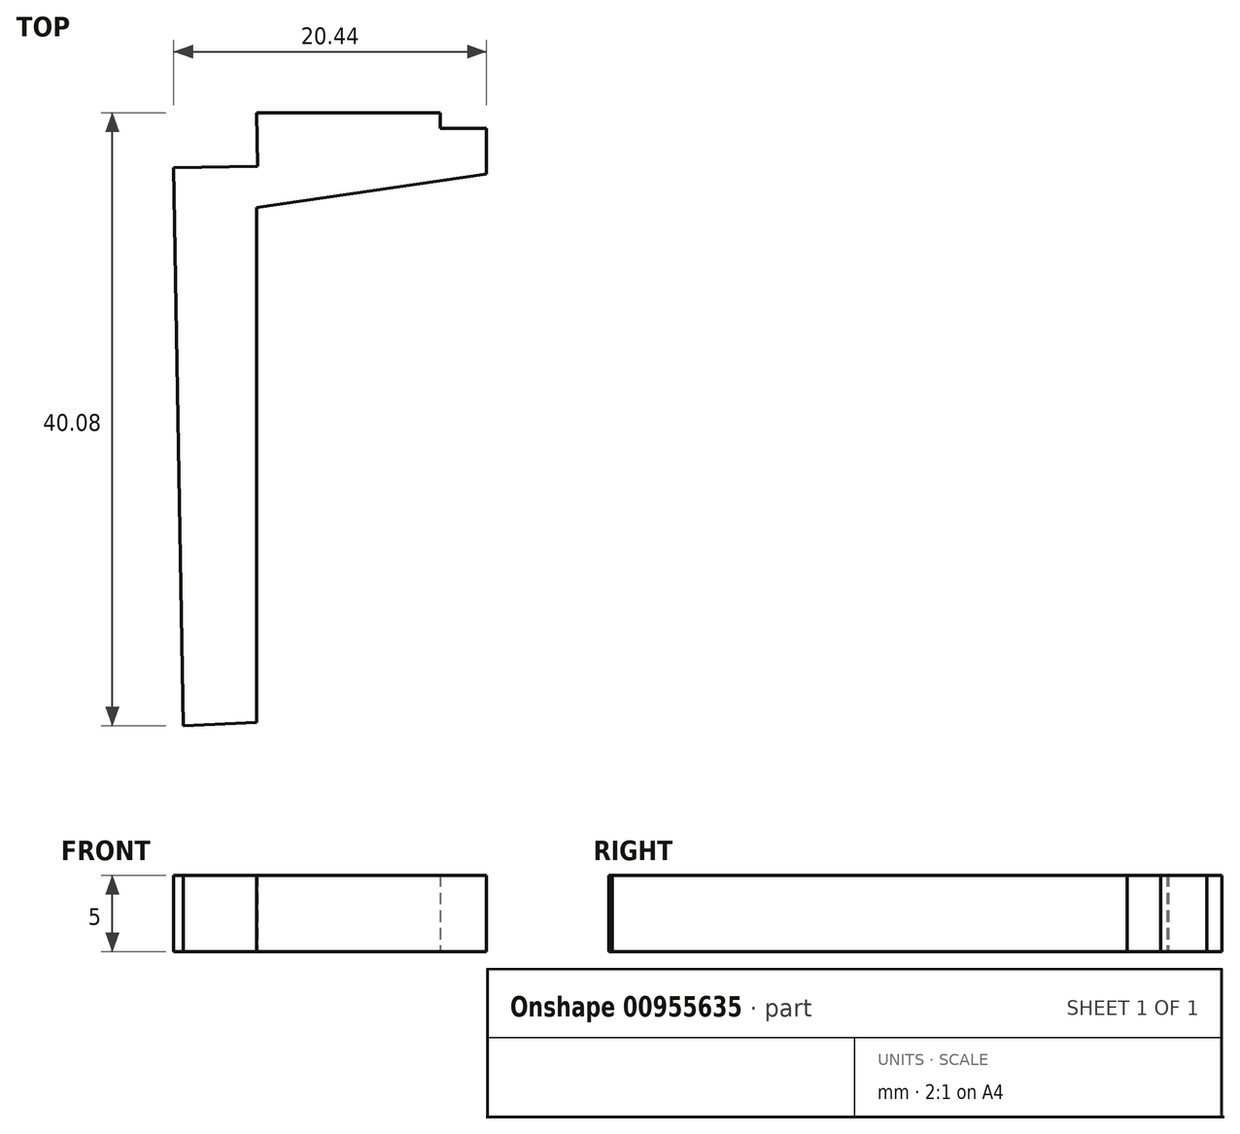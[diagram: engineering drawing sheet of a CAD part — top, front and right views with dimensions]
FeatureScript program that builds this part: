
annotation { "Feature Type Name" : "Feature", "Feature Type Description" : "" }
export const myFeature = defineFeature(function(context is Context, id is Id, definition is map)
    precondition{}
    {
        {
            var Q0;
            Q0=qCreatedBy(makeId("Top.planeOp"),FACE);
            var sketch = newSketch(context, id + "F0", { "sketchPlane" : qUnion([Q0])});
            skLineSegment(sketch, "E0", {"start": v(0.16, -3.6) * mm, "end": v(0.8, -40.08) * mm});
            skLineSegment(sketch, "E1", {"start": v(5.6, 0) * mm, "end": v(5.66, -3.5) * mm, "construction": true});
            skLineSegment(sketch, "E2", {"start": v(5.66, -3.5) * mm, "end": v(0.16, -3.6) * mm, "construction": true});
            skLineSegment(sketch, "E3", {"start": v(5.6, 0) * mm, "end": v(17.6, 0) * mm});
            skLineSegment(sketch, "E4", {"start": v(20.6, -1) * mm, "end": v(20.6, -4) * mm});
            skLineSegment(sketch, "E5", {"start": v(20.6, -4) * mm, "end": v(5.6, -6.2) * mm});
            skLineSegment(sketch, "E6", {"start": v(5.6, -6.2) * mm, "end": v(5.6, -39.85) * mm});
            skLineSegment(sketch, "E7", {"start": v(5.6, -39.85) * mm, "end": v(0.8, -40.08) * mm});
            skLineSegment(sketch, "E8", {"start": v(0.16, -3.6) * mm, "end": v(5.66, -3.5) * mm});
            skLineSegment(sketch, "E9", {"start": v(5.6, 0) * mm, "end": v(5.66, -3.5) * mm});
            skLineSegment(sketch, "E10", {"start": v(20.6, -1) * mm, "end": v(17.6, -1) * mm});
            skLineSegment(sketch, "E11", {"start": v(17.6, -1) * mm, "end": v(17.6, 0) * mm});
            skPoint(sketch, "E12.start.orphan", {"position": v(20.6, 0) * mm});
            skSolve(sketch);
        }
        {
            var Q0;
            Q0 = qSketchRegion(id + "F0", true);
            extrude(context, id + "F1", {"entities" : qUnion([Q0]), "depth" : 5 * mm, "offsetDistance" : 25 * mm, "symmetric" : true});
        }
    });
